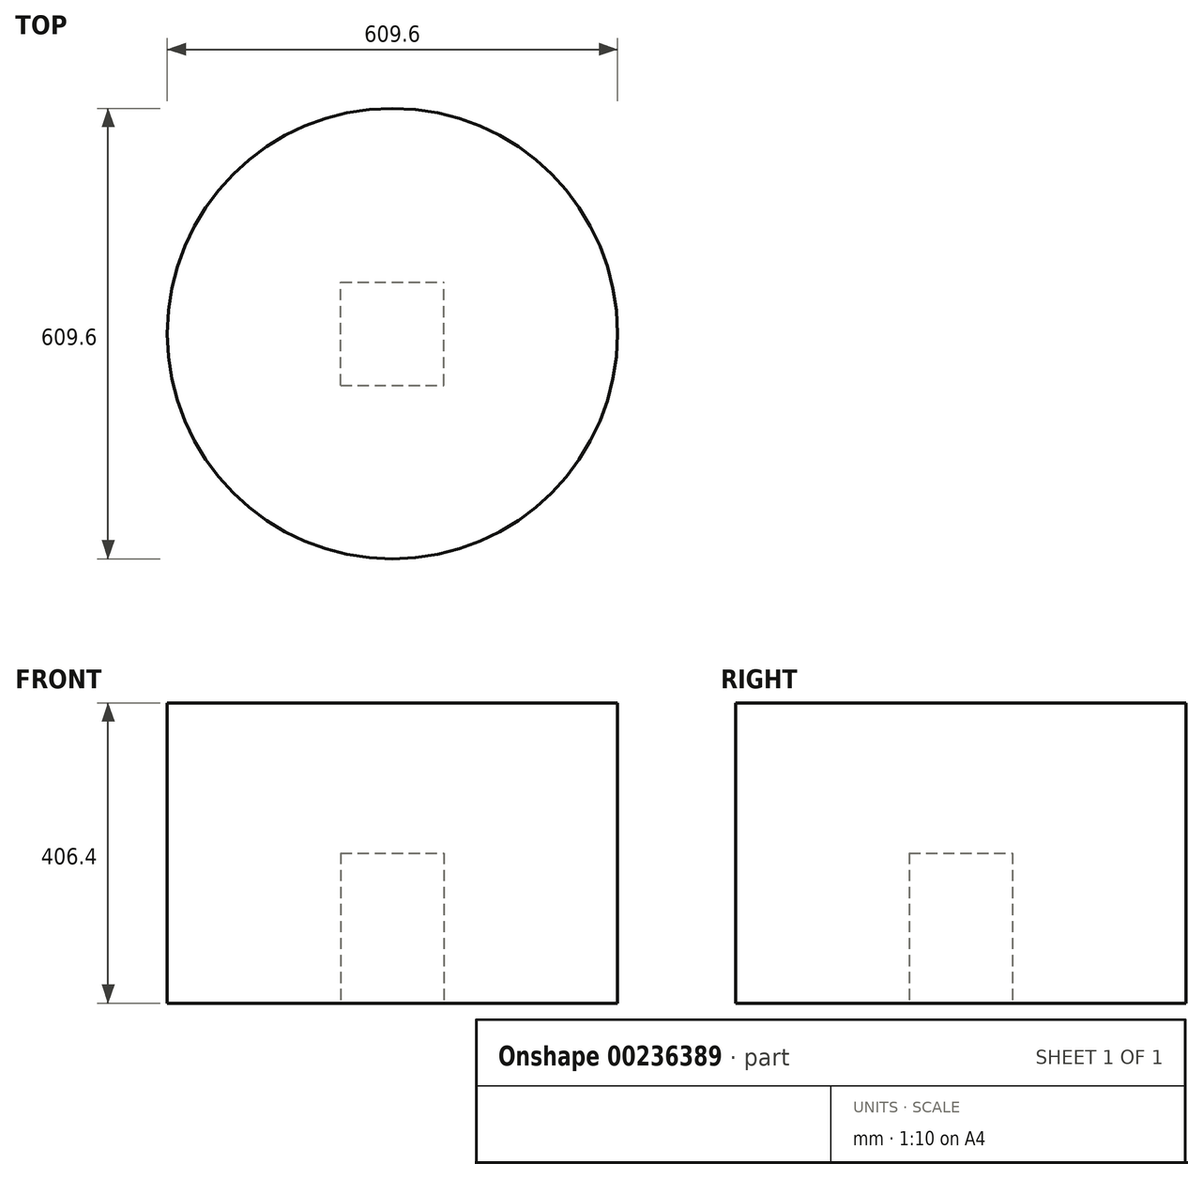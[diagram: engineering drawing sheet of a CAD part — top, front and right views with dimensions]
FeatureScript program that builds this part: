
annotation { "Feature Type Name" : "Feature", "Feature Type Description" : "" }
export const myFeature = defineFeature(function(context is Context, id is Id, definition is map)
    precondition{}
    {
        {
            var Q0;
            Q0=qCreatedBy(makeId("Top.planeOp"),FACE);
            var sketch = newSketch(context, id + "F0", { "sketchPlane" : qUnion([Q0])});
            skCircle(sketch, "E0", {"center": v(0, 0) * mm, "radius": 304.8 * mm});
            skSolve(sketch);
        }
        {
            var Q0;
            Q0=makeQuery(id+"F0.imprint","IMPRINT",FACE,{"disambiguationData":[TD([[makeQuery(id+"F0.imprint","IMPRINT",EDGE,{"derivedFrom":sQuery(id+"F0.wireOp",EDGE,"E0")}),1.0]])]});
            extrude(context, id + "F1", {"entities" : qUnion([Q0]), "depth" : 406.4 * mm});
        }
        {
            var Q0;
            Q0=makeQuery(id+"F1.opExtrude","CAP_FACE",FACE,{"disambiguationData":[OSD([sQuery(id+"F0.wireOp",EDGE,"E0")])],"isStart":true});
            var sketch = newSketch(context, id + "F2", { "sketchPlane" : qUnion([Q0])});
            skLineSegment(sketch, "E1.bottom", {"start": v(-69.85, 69.85) * mm, "end": v(69.85, 69.85) * mm});
            skLineSegment(sketch, "E1.top", {"start": v(-69.85, -69.85) * mm, "end": v(69.85, -69.85) * mm});
            skLineSegment(sketch, "E1.left", {"start": v(-69.85, 69.85) * mm, "end": v(-69.85, -69.85) * mm});
            skLineSegment(sketch, "E1.right", {"start": v(69.85, 69.85) * mm, "end": v(69.85, -69.85) * mm});
            skSolve(sketch);
        }
        {
            var Q0;
            Q0=makeQuery(id+"F2.imprint","IMPRINT",FACE,{"disambiguationData":[TD([[makeQuery(id+"F2.imprint","IMPRINT",EDGE,{"derivedFrom":sQuery(id+"F2.wireOp",EDGE,"E1.bottom")}),-1.0]])]});
            extrude(context, id + "F3", {"entities" : qUnion([Q0]), "operationType" : NewBodyOperationType.REMOVE, "oppositeDirection" : true, "depth" : 203.2 * mm});
        }
    });
